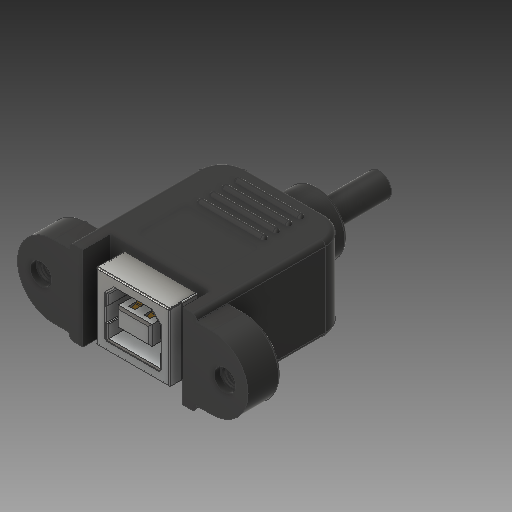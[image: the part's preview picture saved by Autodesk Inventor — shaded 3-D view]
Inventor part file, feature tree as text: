
AUTODESK INVENTOR PART (.ipt)
format: ipt  version: 2019 (Build 230136000, 136)  size: 840,192 bytes
history: native  units: mm
features: other x6, thread x1
ambient origin geometry x8: Origin, YZ Plane, XZ Plane, XY Plane, X Axis, Y Axis, Z Axis, Center Point
bodies: Solid1 (feature_tree), Solid2 (feature_tree), Solid3 (feature_tree), Solid4 (feature_tree), Solid5 (feature_tree), Solid6 (feature_tree), Solid7 (feature_tree)
feature tree (7):
  other  "Type B-1-solid1"
  other  "Type B-1-solid2"
  other  "Type B-1-solid3"
  other  "Type B-1-solid4"
  other  "Type B-1-solid5"
  other  "Type B-1-solid6"
  thread  "Thread2"  [1 undecoded]
note: 1 required parameter value undecoded (feature->parameter linkage not recoverable at this tier; creation-order binding heuristic only, values carry confidence <= 0.55)
